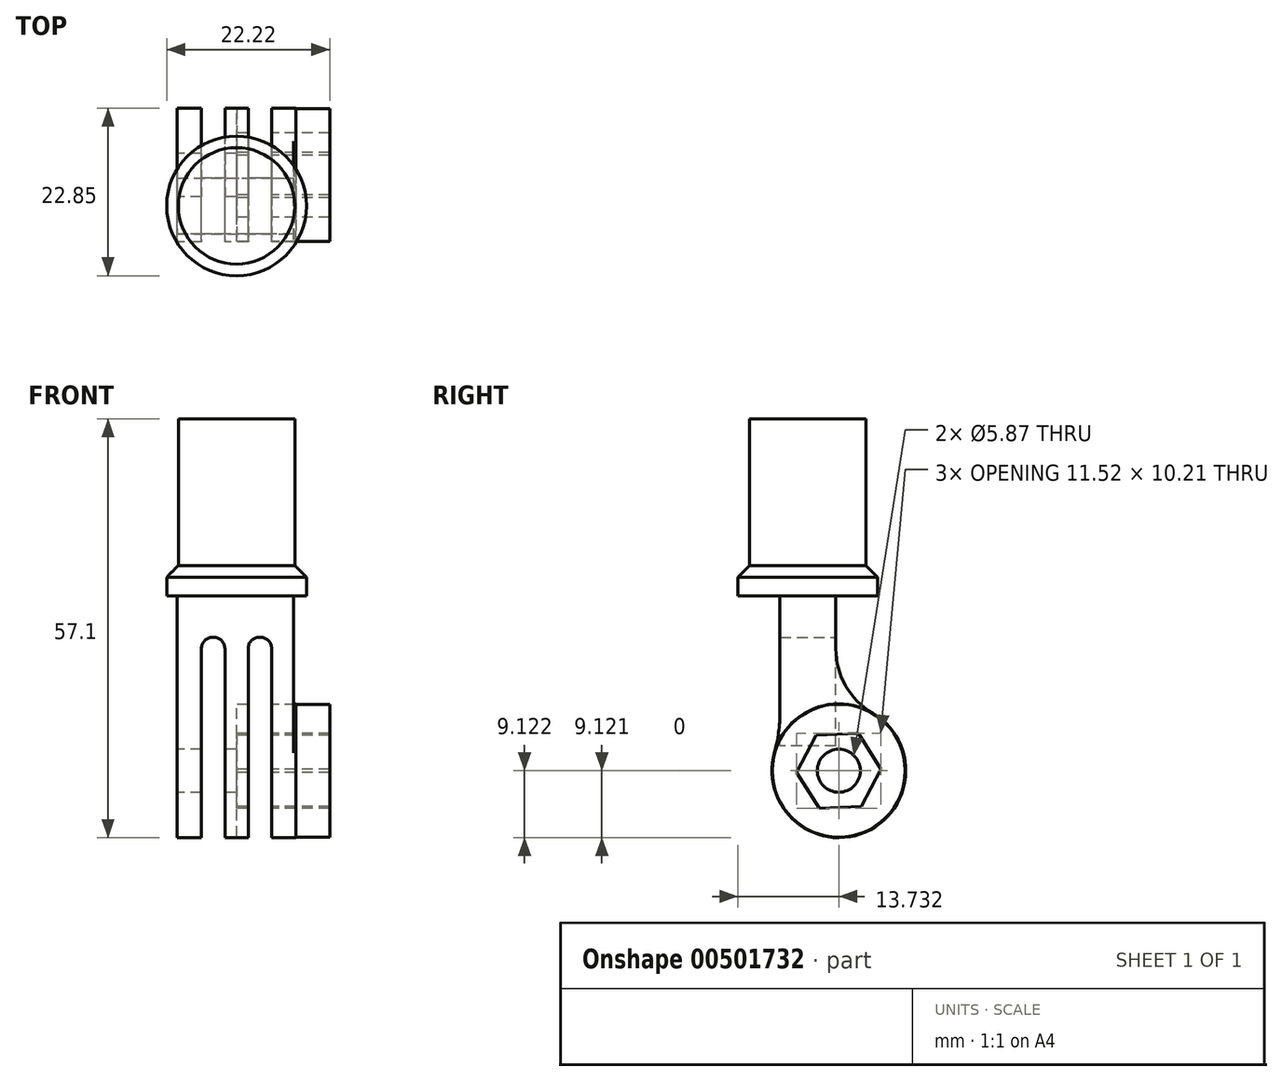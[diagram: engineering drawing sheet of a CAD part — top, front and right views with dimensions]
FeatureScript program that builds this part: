
annotation { "Feature Type Name" : "Feature", "Feature Type Description" : "" }
export const myFeature = defineFeature(function(context is Context, id is Id, definition is map)
    precondition{}
    {
        {
            var Q0;
            Q0=qCreatedBy(makeId("Top.planeOp"),FACE);
            var sketch = newSketch(context, id + "F0", { "sketchPlane" : qUnion([Q0])});
            skCircle(sketch, "E0", {"center": v(0, 0) * mm, "radius": 7.94 * mm});
            skSolve(sketch);
        }
        {
            var Q0;
            Q0=makeQuery(id+"F0.imprint","IMPRINT",FACE,{"disambiguationData":[TD([[makeQuery(id+"F0.imprint","IMPRINT",EDGE,{"derivedFrom":sQuery(id+"F0.wireOp",EDGE,"E0")}),1.0]])]});
            extrude(context, id + "F1", {"entities" : qUnion([Q0]), "depth" : 19.05 * mm});
        }
        {
            var Q0;
            Q0=qCreatedBy(makeId("Top.planeOp"),FACE);
            var sketch = newSketch(context, id + "F2", { "sketchPlane" : qUnion([Q0])});
            skCircle(sketch, "E1", {"center": v(0, 0) * mm, "radius": 9.52 * mm});
            skSolve(sketch);
        }
        {
            var Q0;
            Q0=makeQuery(id+"F2.imprint","IMPRINT",FACE,{"disambiguationData":[TD([[makeQuery(id+"F2.imprint","IMPRINT",EDGE,{"derivedFrom":sQuery(id+"F2.wireOp",EDGE,"E1")}),1.0]])]});
            extrude(context, id + "F3", {"entities" : qUnion([Q0]), "operationType" : NewBodyOperationType.ADD, "depth" : -2.54 * mm});
        }
        {
            var Q0;
            Q0=makeQuery(id+"F3.opExtrude","CAP_EDGE",EDGE,{"disambiguationData":[OSD([sQuery(id+"F2.wireOp",EDGE,"E1")])],"isStart":true});
            chamfer(context, id + "F4", {"entities" : qUnion([Q0]), "width" : 2.54 * mm, "tangentPropagation" : true});
        }
        {
            var Q0;
            Q0=makeQuery(id+"F3.opExtrude","CAP_FACE",FACE,{"disambiguationData":[OSD([sQuery(id+"F2.wireOp",EDGE,"E1")])],"isStart":false});
            extrude(context, id + "F5", {"entities" : qUnion([Q0]), "depth" : 2.54 * mm});
        }
        {
            var Q0;
            Q0=qCreatedBy(makeId("Front.planeOp"),FACE);
            var sketch = newSketch(context, id + "F6", { "sketchPlane" : qUnion([Q0])});
            skLineSegment(sketch, "E2.bottom", {"start": v(7.8, -25.52) * mm, "end": v(-8.09, -25.52) * mm});
            skLineSegment(sketch, "E2.top", {"start": v(7.8, -4.81) * mm, "end": v(-8.09, -4.81) * mm});
            skLineSegment(sketch, "E2.left", {"start": v(7.8, -25.52) * mm, "end": v(7.8, -4.81) * mm});
            skLineSegment(sketch, "E2.right", {"start": v(-8.09, -25.52) * mm, "end": v(-8.09, -4.81) * mm});
            skLineSegment(sketch, "E3.left", {"start": v(7.8, -4.81) * mm, "end": v(7.8, -25.52) * mm});
            skLineSegment(sketch, "E3.right", {"start": v(-8.09, -4.81) * mm, "end": v(-8.09, -25.52) * mm});
            skSolve(sketch);
        }
        {
            var Q0;
            Q0=makeQuery(id+"F6.imprint","IMPRINT",FACE,{"disambiguationData":[TD([[makeQuery(id+"F6.imprint","IMPRINT",EDGE,{"derivedFrom":sQuery(id+"F6.wireOp",EDGE,"E2.top")}),1.0]])]});
            extrude(context, id + "F7", {"entities" : qUnion([Q0]), "operationType" : NewBodyOperationType.ADD, "endBound" : BoundingType.SYMMETRIC, "depth" : 7.62 * mm});
        }
        {
            var Q0;
            Q0=qCreatedBy(makeId("Right.planeOp"),FACE);
            var sketch = newSketch(context, id + "F8", { "sketchPlane" : qUnion([Q0])});
            skCircle(sketch, "E4", {"center": v(4.21, -28.93) * mm, "radius": 9.12 * mm});
            skCircle(sketch, "E5", {"center": v(4.21, -28.93) * mm, "radius": 2.94 * mm});
            skSolve(sketch);
        }
        {
            var Q0;
            Q0=makeQuery(id+"F8.imprint","IMPRINT",FACE,{"disambiguationData":[TD([[makeQuery(id+"F8.imprint","IMPRINT",EDGE,{"derivedFrom":sQuery(id+"F8.wireOp",EDGE,"E4")}),1.0]])]});
            extrude(context, id + "F9", {"entities" : qUnion([Q0]), "operationType" : NewBodyOperationType.ADD, "endBound" : BoundingType.SYMMETRIC, "depth" : 16.15 * mm});
        }
        {
            var Q0;
            Q0=makeQuery(id+"F9.boolean.opBoolean","INTERSECT",EDGE,{"derivedFrom":[makeQuery(id+"F7.opExtrude","CAP_FACE",FACE,{"disambiguationData":[OSD([sQuery(id+"F6.wireOp",EDGE,"E2.top"),sQuery(id+"F6.wireOp",EDGE,"E2.bottom"),sQuery(id+"F6.wireOp",EDGE,"E3.left"),sQuery(id+"F6.wireOp",EDGE,"E3.right")])],"isStart":true}),makeQuery(id+"F9.opExtrude","SWEPT_FACE",FACE,{"disambiguationData":[OSD([sQuery(id+"F8.wireOp",EDGE,"E4")])]})]});
            fillet(context, id + "F10", {"entities" : qUnion([Q0]), "radius" : 10.13 * mm, "tangentPropagation" : true, "allowEdgeOverflow" : false});
        }
        {
            var Q0;
            Q0=makeQuery(id+"F9.boolean.opBoolean","INTERSECT",EDGE,{"derivedFrom":[makeQuery(id+"F7.opExtrude","CAP_FACE",FACE,{"disambiguationData":[OSD([sQuery(id+"F6.wireOp",EDGE,"E2.top"),sQuery(id+"F6.wireOp",EDGE,"E2.bottom"),sQuery(id+"F6.wireOp",EDGE,"E3.left"),sQuery(id+"F6.wireOp",EDGE,"E3.right")])],"isStart":false}),makeQuery(id+"F9.opExtrude","SWEPT_FACE",FACE,{"disambiguationData":[OSD([sQuery(id+"F8.wireOp",EDGE,"E4")])]})]});
            fillet(context, id + "F11", {"entities" : qUnion([Q0]), "radius" : 20.94 * mm, "tangentPropagation" : true, "allowEdgeOverflow" : false});
        }
        {
            var Q0;
            Q0=qCreatedBy(makeId("Front.planeOp"),FACE);
            var sketch = newSketch(context, id + "F12", { "sketchPlane" : qUnion([Q0])});
            skLineSegment(sketch, "E6.bottom", {"start": v(-1.59, -10.74) * mm, "end": v(-4.79, -10.74) * mm});
            skLineSegment(sketch, "E6.top", {"start": v(-1.59, -38.3) * mm, "end": v(-4.79, -38.3) * mm});
            skLineSegment(sketch, "E6.left", {"start": v(-1.59, -10.74) * mm, "end": v(-1.59, -38.3) * mm});
            skLineSegment(sketch, "E6.right", {"start": v(-4.79, -10.74) * mm, "end": v(-4.79, -38.3) * mm});
            skLineSegment(sketch, "E7.bottom", {"start": v(1.58, -10.73) * mm, "end": v(4.78, -10.73) * mm});
            skLineSegment(sketch, "E7.top", {"start": v(1.58, -38.32) * mm, "end": v(4.78, -38.32) * mm});
            skLineSegment(sketch, "E7.left", {"start": v(1.58, -10.73) * mm, "end": v(1.58, -38.32) * mm});
            skLineSegment(sketch, "E7.right", {"start": v(4.78, -10.73) * mm, "end": v(4.78, -38.32) * mm});
            skSolve(sketch);
        }
        {
            var Q0;
            Q0=qCreatedBy(makeId("Right.planeOp"),FACE);
            var sketch = newSketch(context, id + "F13", { "sketchPlane" : qUnion([Q0])});
            skCircle(sketch, "E8", {"center": v(4.2, -28.92) * mm, "radius": 9.06 * mm});
            skSolve(sketch);
        }
        {
            var Q0;
            Q0=qCreatedBy(makeId("Right.planeOp"),FACE);
            var sketch = newSketch(context, id + "F14", { "sketchPlane" : qUnion([Q0])});
            skCircle(sketch, "E9.cCircle", {"center": v(4.21, -28.93) * mm, "radius": 5 * mm, "construction": true});
            skLineSegment(sketch, "E9.0", {"start": v(9.97, -28.7) * mm, "end": v(7.3, -33.8) * mm});
            skLineSegment(sketch, "E9.1", {"start": v(7.3, -33.8) * mm, "end": v(1.54, -34.04) * mm});
            skLineSegment(sketch, "E9.2", {"start": v(1.54, -34.04) * mm, "end": v(-1.55, -29.16) * mm});
            skLineSegment(sketch, "E9.3", {"start": v(-1.55, -29.16) * mm, "end": v(1.13, -24.06) * mm});
            skLineSegment(sketch, "E9.4", {"start": v(1.13, -24.06) * mm, "end": v(6.89, -23.82) * mm});
            skLineSegment(sketch, "E9.5", {"start": v(6.89, -23.82) * mm, "end": v(9.97, -28.7) * mm});
            skPoint(sketch, "E9.0.midPoint", {"position": v(8.63, -31.25) * mm});
            skSolve(sketch);
        }
        {
            var Q0;
            Q0 = qSketchRegion(id + "F13", true);
            extrude(context, id + "F15", {"entities" : qUnion([Q0]), "depth" : 12.7 * mm});
        }
        {
            var Q0;
            Q0 = qSketchRegion(id + "F14", true);
            extrude(context, id + "F16", {"entities" : qUnion([Q0]), "operationType" : NewBodyOperationType.REMOVE, "depth" : 12.7 * mm});
        }
        {
            var Q0;
            Q0=makeQuery(id+"F12.imprint","IMPRINT",FACE,{"disambiguationData":[TD([[makeQuery(id+"F12.imprint","IMPRINT",EDGE,{"derivedFrom":sQuery(id+"F12.wireOp",EDGE,"E7.bottom")}),-1.0]])]});
            var Q1;
            Q1=makeQuery(id+"F12.imprint","IMPRINT",FACE,{"disambiguationData":[TD([[makeQuery(id+"F12.imprint","IMPRINT",EDGE,{"derivedFrom":sQuery(id+"F12.wireOp",EDGE,"E6.bottom")}),1.0]])]});
            extrude(context, id + "F17", {"entities" : qUnion([Q0, Q1]), "operationType" : NewBodyOperationType.REMOVE, "endBound" : BoundingType.SYMMETRIC, "depth" : 35.3 * mm});
        }
        {
            var Q0;
            Q0=makeQuery(id+"F17.boolean.opBoolean","COPY",EDGE,{"derivedFrom":makeQuery(id+"F17.opExtrude","SWEPT_EDGE",EDGE,{"disambiguationData":[OSD([sQuery(id+"F12.wireOp",EDGE,"E7.bottom"),sQuery(id+"F12.wireOp",EDGE,"E7.left")])]})});
            var Q1;
            Q1=makeQuery(id+"F17.boolean.opBoolean","COPY",EDGE,{"derivedFrom":makeQuery(id+"F17.opExtrude","SWEPT_EDGE",EDGE,{"disambiguationData":[OSD([sQuery(id+"F12.wireOp",EDGE,"E7.bottom"),sQuery(id+"F12.wireOp",EDGE,"E7.right")])]})});
            var Q2;
            Q2=makeQuery(id+"F17.boolean.opBoolean","COPY",EDGE,{"derivedFrom":makeQuery(id+"F17.opExtrude","SWEPT_EDGE",EDGE,{"disambiguationData":[OSD([sQuery(id+"F12.wireOp",EDGE,"E6.bottom"),sQuery(id+"F12.wireOp",EDGE,"E6.left")])]})});
            var Q3;
            Q3=makeQuery(id+"F17.boolean.opBoolean","COPY",EDGE,{"derivedFrom":makeQuery(id+"F17.opExtrude","SWEPT_EDGE",EDGE,{"disambiguationData":[OSD([sQuery(id+"F12.wireOp",EDGE,"E6.bottom"),sQuery(id+"F12.wireOp",EDGE,"E6.right")])]})});
            fillet(context, id + "F18", {"entities" : qUnion([Q0, Q1, Q2, Q3]), "radius" : 1.53 * mm, "tangentPropagation" : true, "allowEdgeOverflow" : false});
        }
    });
